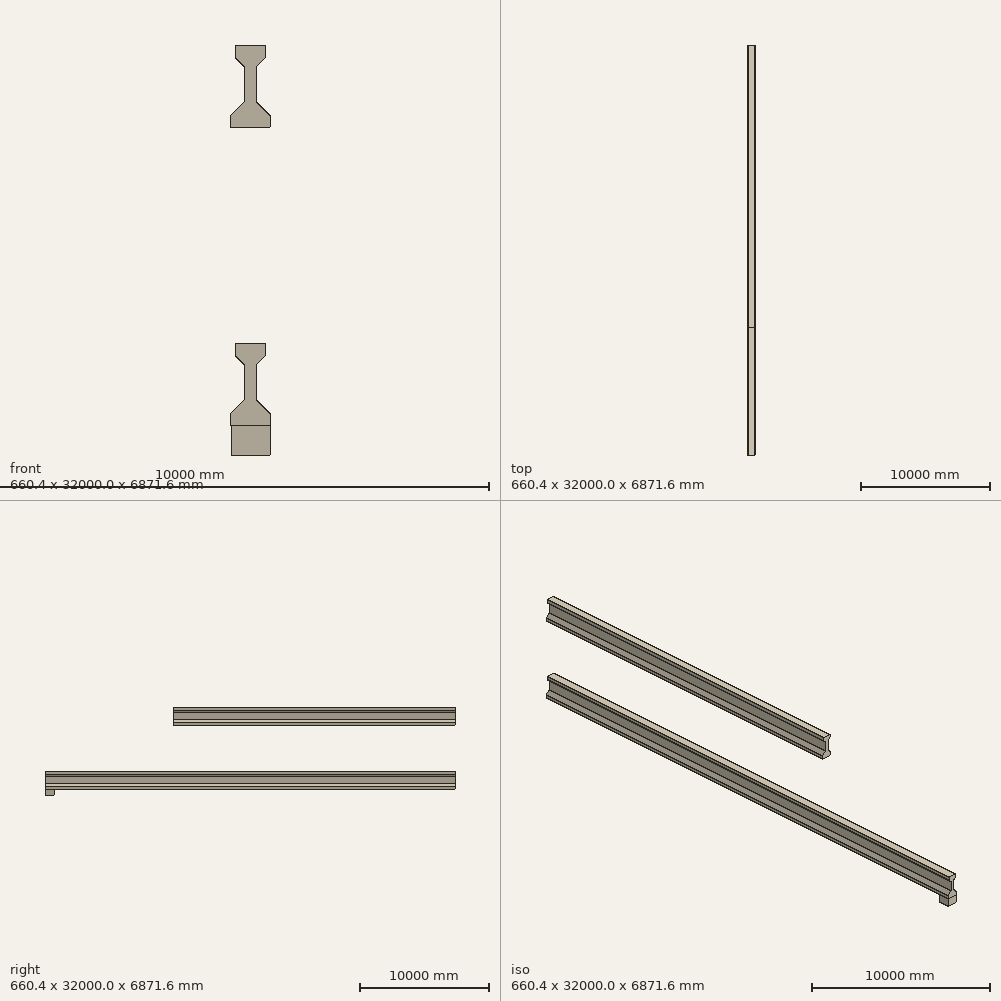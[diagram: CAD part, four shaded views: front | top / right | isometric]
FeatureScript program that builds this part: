
annotation { "Feature Type Name" : "Feature", "Feature Type Description" : "" }
export const myFeature = defineFeature(function(context is Context, id is Id, definition is map)
    precondition{}
    {
        {
            var Q0;
            Q0=qCreatedBy(makeId("Front.planeOp"),FACE);
            var sketch = newSketch(context, id + "F0", { "sketchPlane" : qUnion([Q0])});
            skLineSegment(sketch, "E0", {"start": v(0, 1444.94) * mm, "end": v(-254, 1444.94) * mm});
            skLineSegment(sketch, "E1", {"start": v(-254, 1444.94) * mm, "end": v(-254, 1241.74) * mm});
            skLineSegment(sketch, "E2", {"start": v(-254, 1241.74) * mm, "end": v(-101.6, 1089.34) * mm});
            skLineSegment(sketch, "E3", {"start": v(-101.6, 1089.34) * mm, "end": v(-101.6, 505.14) * mm});
            skLineSegment(sketch, "E4", {"start": v(-101.6, 505.14) * mm, "end": v(-330.2, 276.54) * mm});
            skLineSegment(sketch, "E5", {"start": v(-330.2, 276.54) * mm, "end": v(-330.2, 73.34) * mm});
            skLineSegment(sketch, "E6", {"start": v(-330.2, 73.34) * mm, "end": v(0, 73.34) * mm});
            skLineSegment(sketch, "E7.MirrorCS", {"start": v(0, 1444.94) * mm, "end": v(254, 1444.94) * mm});
            skLineSegment(sketch, "E8.MirrorCS", {"start": v(254, 1444.94) * mm, "end": v(254, 1241.74) * mm});
            skLineSegment(sketch, "E9.MirrorCS", {"start": v(254, 1241.74) * mm, "end": v(101.6, 1089.34) * mm});
            skLineSegment(sketch, "E10.MirrorCS", {"start": v(101.6, 1089.34) * mm, "end": v(101.6, 505.14) * mm});
            skLineSegment(sketch, "E11.MirrorCS", {"start": v(101.6, 505.14) * mm, "end": v(330.2, 276.54) * mm});
            skLineSegment(sketch, "E12.MirrorCS", {"start": v(330.2, 276.54) * mm, "end": v(330.2, 73.34) * mm});
            skLineSegment(sketch, "E13.MirrorCS", {"start": v(330.2, 73.34) * mm, "end": v(0, 73.34) * mm});
            skSolve(sketch);
        }
        {
            var Q0;
            Q0=makeQuery(id+"F0.imprint","IMPRINT",FACE,{"disambiguationData":[TD([[makeQuery(id+"F0.imprint","IMPRINT",EDGE,{"derivedFrom":sQuery(id+"F0.wireOp",EDGE,"E0")}),1.0]])]});
            extrude(context, id + "F1", {"entities" : qUnion([Q0]), "depth" : 32000 * mm});
        }
        {
            var Q0;
            Q0=makeQuery(id+"F1.opExtrude","SWEPT_FACE",FACE,{"disambiguationData":[OSD([sQuery(id+"F0.wireOp",EDGE,"E6"),sQuery(id+"F0.wireOp",EDGE,"E13.MirrorCS")])]});
            var sketch = newSketch(context, id + "F2", { "sketchPlane" : qUnion([Q0])});
            skLineSegment(sketch, "E14", {"start": v(0, 0) * mm, "end": v(0, 500) * mm});
            skPoint(sketch, "E14.endSnap0", {"position": v(0, 0) * mm});
            skLineSegment(sketch, "E15", {"start": v(0, 500) * mm, "end": v(-330.2, 500) * mm});
            skSolve(sketch);
        }
        {
            var Q0;
            {var subQ5=sQuery(id+"F2.wireOp",EDGE,"E14");Q0=makeQuery(id+"F2.imprint","IMPRINT",FACE,{"disambiguationData":[TD([[makeQuery(id+"F2.imprint","IMPRINT",EDGE,{"derivedFrom":subQ5}),-1.0]])]});}
            var sketch = newSketch(context, id + "F3", { "sketchPlane" : qUnion([Q0])});
            skLineSegment(sketch, "E16", {"start": v(-326.71, 31993.95) * mm, "end": v(-326.71, 31333.55) * mm});
            skLineSegment(sketch, "E17", {"start": v(-326.71, 31333.55) * mm, "end": v(333.69, 31333.55) * mm});
            skLineSegment(sketch, "E18", {"start": v(333.69, 31333.55) * mm, "end": v(333.69, 31993.95) * mm});
            skLineSegment(sketch, "E19", {"start": v(333.69, 31993.95) * mm, "end": v(-326.71, 31993.95) * mm});
            skSolve(sketch);
        }
        {
            var Q0;
            {var subQ0=sQuery(id+"F3.wireOp",EDGE,"E16");Q0=makeQuery(id+"F3.imprint","IMPRINT",FACE,{"disambiguationData":[TD([[makeQuery(id+"F3.imprint","IMPRINT",EDGE,{"derivedFrom":subQ0}),1.0]])]});}
            extrude(context, id + "F4", {"entities" : qUnion([Q0]), "depth" : 500 * mm});
        }
        {
            var Q0;
            Q0=makeQuery(id+"F1.opExtrude","SWEPT_BODY",BODY,{"disambiguationData":[OSD([sQuery(id+"F0.wireOp",EDGE,"E0"),sQuery(id+"F0.wireOp",EDGE,"E1"),sQuery(id+"F0.wireOp",EDGE,"E2"),sQuery(id+"F0.wireOp",EDGE,"E3"),sQuery(id+"F0.wireOp",EDGE,"E4"),sQuery(id+"F0.wireOp",EDGE,"E5"),sQuery(id+"F0.wireOp",EDGE,"E6"),sQuery(id+"F0.wireOp",EDGE,"E7.MirrorCS"),sQuery(id+"F0.wireOp",EDGE,"E8.MirrorCS"),sQuery(id+"F0.wireOp",EDGE,"E9.MirrorCS"),sQuery(id+"F0.wireOp",EDGE,"E10.MirrorCS"),sQuery(id+"F0.wireOp",EDGE,"E11.MirrorCS"),sQuery(id+"F0.wireOp",EDGE,"E12.MirrorCS"),sQuery(id+"F0.wireOp",EDGE,"E13.MirrorCS")])]});
            transform(context, id + "F5", {"entities" : qUnion([Q0]), "transformType" : TransformType.TRANSLATION_3D, "dx" : 0 * mm, "dy" : 0 * mm, "dz" : 5000 * mm, "makeCopy" : true});
        }
        {
            var Q0;
            Q0=makeQuery(id+"F5.opPattern","COPY",FACE,{"derivedFrom":makeQuery(id+"F1.opExtrude","CAP_FACE",FACE,{"disambiguationData":[OSD([sQuery(id+"F0.wireOp",EDGE,"E0"),sQuery(id+"F0.wireOp",EDGE,"E1"),sQuery(id+"F0.wireOp",EDGE,"E2"),sQuery(id+"F0.wireOp",EDGE,"E3"),sQuery(id+"F0.wireOp",EDGE,"E4"),sQuery(id+"F0.wireOp",EDGE,"E5"),sQuery(id+"F0.wireOp",EDGE,"E6"),sQuery(id+"F0.wireOp",EDGE,"E7.MirrorCS"),sQuery(id+"F0.wireOp",EDGE,"E8.MirrorCS"),sQuery(id+"F0.wireOp",EDGE,"E9.MirrorCS"),sQuery(id+"F0.wireOp",EDGE,"E10.MirrorCS"),sQuery(id+"F0.wireOp",EDGE,"E11.MirrorCS"),sQuery(id+"F0.wireOp",EDGE,"E12.MirrorCS"),sQuery(id+"F0.wireOp",EDGE,"E13.MirrorCS")])],"isStart":false}),"instanceName":"1"});
            extrude(context, id + "F6", {"entities" : qUnion([Q0]), "operationType" : NewBodyOperationType.REMOVE, "oppositeDirection" : true, "depth" : 12000 * mm});
        }
        {
            var Q0;
            Q0=makeQuery(id+"F6.boolean.opBoolean","COPY",FACE,{"derivedFrom":makeQuery(id+"F6.opExtrude","CAP_FACE",FACE,{"disambiguationData":[OSD([sQuery(id+"F0.wireOp",EDGE,"E0"),sQuery(id+"F0.wireOp",EDGE,"E1"),sQuery(id+"F0.wireOp",EDGE,"E2"),sQuery(id+"F0.wireOp",EDGE,"E3"),sQuery(id+"F0.wireOp",EDGE,"E4"),sQuery(id+"F0.wireOp",EDGE,"E5"),sQuery(id+"F0.wireOp",EDGE,"E6"),sQuery(id+"F0.wireOp",EDGE,"E7.MirrorCS"),sQuery(id+"F0.wireOp",EDGE,"E8.MirrorCS"),sQuery(id+"F0.wireOp",EDGE,"E9.MirrorCS"),sQuery(id+"F0.wireOp",EDGE,"E10.MirrorCS"),sQuery(id+"F0.wireOp",EDGE,"E11.MirrorCS"),sQuery(id+"F0.wireOp",EDGE,"E12.MirrorCS"),sQuery(id+"F0.wireOp",EDGE,"E13.MirrorCS")])],"isStart":false})});
            extrude(context, id + "F7", {"entities" : qUnion([Q0]), "operationType" : NewBodyOperationType.ADD, "depth" : 2000 * mm});
        }
    });
